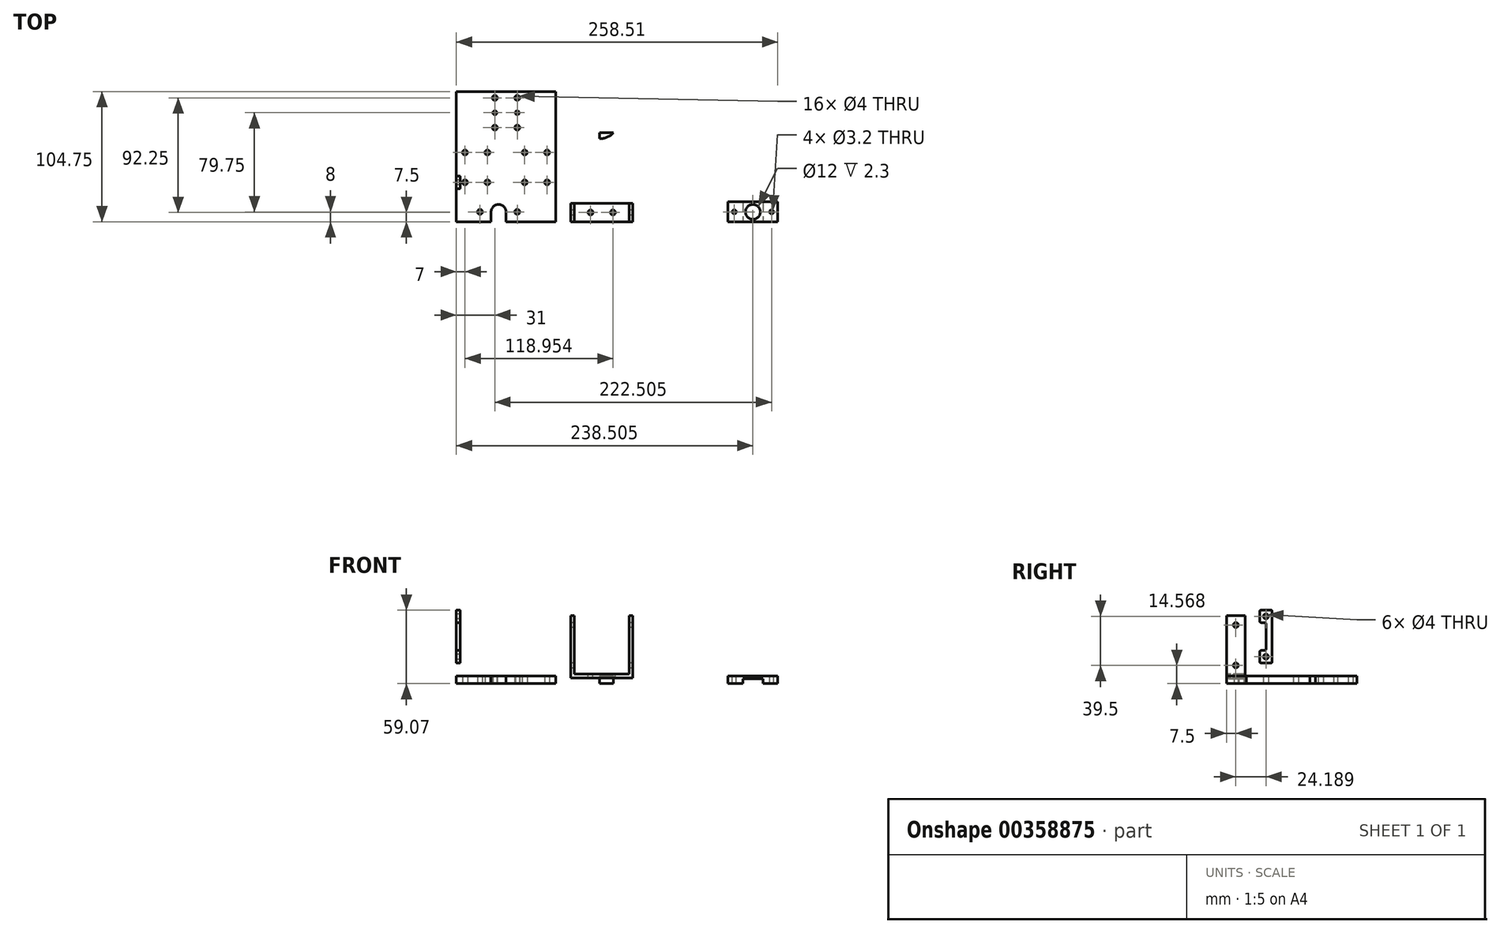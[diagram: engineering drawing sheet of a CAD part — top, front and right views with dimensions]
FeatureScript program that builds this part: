
annotation { "Feature Type Name" : "Feature", "Feature Type Description" : "" }
export const myFeature = defineFeature(function(context is Context, id is Id, definition is map)
    precondition{}
    {
        {
            var Q0;
            Q0=qCreatedBy(makeId("Front.planeOp"),FACE);
            var sketch = newSketch(context, id + "F0", { "sketchPlane" : qUnion([Q0])});
            skLineSegment(sketch, "E0", {"start": v(91.95, 4.57) * mm, "end": v(91.95, 54.57) * mm});
            skLineSegment(sketch, "E1", {"start": v(91.95, 54.57) * mm, "end": v(94.95, 54.57) * mm});
            skLineSegment(sketch, "E2", {"start": v(94.95, 54.57) * mm, "end": v(94.95, 7.57) * mm});
            skLineSegment(sketch, "E3", {"start": v(94.95, 7.57) * mm, "end": v(116.95, 7.57) * mm});
            skLineSegment(sketch, "E4", {"start": v(116.95, 4.57) * mm, "end": v(91.95, 4.57) * mm});
            skLineSegment(sketch, "E5.MirrorCS", {"start": v(138.95, 54.57) * mm, "end": v(138.95, 7.57) * mm});
            skLineSegment(sketch, "E6.MirrorCS", {"start": v(141.95, 54.57) * mm, "end": v(138.95, 54.57) * mm});
            skLineSegment(sketch, "E7.MirrorCS", {"start": v(141.95, 4.57) * mm, "end": v(141.95, 54.57) * mm});
            skLineSegment(sketch, "E8.MirrorCS", {"start": v(138.95, 7.57) * mm, "end": v(116.95, 7.57) * mm});
            skLineSegment(sketch, "E9.MirrorCS", {"start": v(116.95, 4.57) * mm, "end": v(141.95, 4.57) * mm});
            skSolve(sketch);
        }
        {
            var Q0;
            Q0=makeQuery(id+"F0.imprint","IMPRINT",FACE,{"disambiguationData":[TD([[makeQuery(id+"F0.imprint","IMPRINT",EDGE,{"derivedFrom":sQuery(id+"F0.wireOp",EDGE,"E0")}),-1.0]])]});
            extrude(context, id + "F1", {"entities" : qUnion([Q0]), "oppositeDirection" : true, "depth" : 15 * mm});
        }
        {
            var Q0;
            Q0=makeQuery(id+"F1.opExtrude","SWEPT_FACE",FACE,{"disambiguationData":[OSD([sQuery(id+"F0.wireOp",EDGE,"E3")])]});
            var sketch = newSketch(context, id + "F2", { "sketchPlane" : qUnion([Q0])});
            skCircle(sketch, "E10", {"center": v(107.95, 7.5) * mm, "radius": 2 * mm});
            skPoint(sketch, "E10.centerSnap0", {"position": v(94.95, 7.5) * mm});
            skCircle(sketch, "E11", {"center": v(125.95, 7.5) * mm, "radius": 2 * mm});
            skLineSegment(sketch, "E12", {"start": v(107.95, 7.5) * mm, "end": v(94.95, 7.5) * mm, "construction": true});
            skLineSegment(sketch, "E13", {"start": v(125.95, 7.5) * mm, "end": v(138.95, 7.5) * mm, "construction": true});
            skSolve(sketch);
        }
        {
            var Q0;
            Q0=makeQuery(id+"F1.opExtrude","SWEPT_FACE",FACE,{"disambiguationData":[OSD([sQuery(id+"F0.wireOp",EDGE,"E0")])]});
            var sketch = newSketch(context, id + "F3", { "sketchPlane" : qUnion([Q0])});
            skCircle(sketch, "E14", {"center": v(-7.5, 14.57) * mm, "radius": 2 * mm});
            skPoint(sketch, "E14.centerSnap0", {"position": v(-7.5, 7.57) * mm});
            skCircle(sketch, "E15", {"center": v(-7.5, 47.07) * mm, "radius": 2 * mm});
            skSolve(sketch);
        }
        {
            var Q0;
            Q0=makeQuery(id+"F3.imprint","IMPRINT",FACE,{"disambiguationData":[TD([[makeQuery(id+"F3.imprint","IMPRINT",EDGE,{"derivedFrom":sQuery(id+"F3.wireOp",EDGE,"E15")}),1.0]])]});
            var Q1;
            Q1=makeQuery(id+"F3.imprint","IMPRINT",FACE,{"disambiguationData":[TD([[makeQuery(id+"F3.imprint","IMPRINT",EDGE,{"derivedFrom":sQuery(id+"F3.wireOp",EDGE,"E14")}),1.0]])]});
            extrude(context, id + "F4", {"entities" : qUnion([Q0, Q1]), "operationType" : NewBodyOperationType.REMOVE, "endBound" : BoundingType.THROUGH_ALL, "oppositeDirection" : true, "depth" : 25 * mm});
        }
        {
            var Q0;
            Q0=makeQuery(id+"F2.imprint","IMPRINT",FACE,{"disambiguationData":[TD([[makeQuery(id+"F2.imprint","IMPRINT",EDGE,{"derivedFrom":sQuery(id+"F2.wireOp",EDGE,"E10")}),1.0]])]});
            var Q1;
            Q1=makeQuery(id+"F2.imprint","IMPRINT",FACE,{"disambiguationData":[TD([[makeQuery(id+"F2.imprint","IMPRINT",EDGE,{"derivedFrom":sQuery(id+"F2.wireOp",EDGE,"E11")}),1.0]])]});
            var Q2;
            Q2=sQuery(id+"F2.wireOp",EDGE,"E10");
            var Q3;
            Q3=sQuery(id+"F2.wireOp",EDGE,"E11");
            extrude(context, id + "F5", {"entities" : qUnion([Q0, Q1]), "operationType" : NewBodyOperationType.REMOVE, "surfaceEntities" : qUnion([Q2, Q3]), "endBound" : BoundingType.UP_TO_NEXT, "oppositeDirection" : true, "depth" : 25 * mm});
        }
        {
            var Q0;
            Q0=qCreatedBy(makeId("Right.planeOp"),FACE);
            var sketch = newSketch(context, id + "F6", { "sketchPlane" : qUnion([Q0])});
            skLineSegment(sketch, "E16.top", {"start": v(26.69, 16.57) * mm, "end": v(36.69, 16.57) * mm});
            skLineSegment(sketch, "E16.right", {"start": v(36.69, 59.07) * mm, "end": v(36.69, 16.57) * mm});
            skCircle(sketch, "E17", {"center": v(31.69, 54.07) * mm, "radius": 2 * mm});
            skCircle(sketch, "E18", {"center": v(31.69, 21.57) * mm, "radius": 2 * mm});
            skLineSegment(sketch, "E19", {"start": v(31.69, 49.07) * mm, "end": v(31.69, 26.57) * mm});
            skLineSegment(sketch, "E20", {"start": v(31.69, 49.07) * mm, "end": v(26.69, 49.07) * mm});
            skLineSegment(sketch, "E21", {"start": v(31.69, 26.57) * mm, "end": v(26.69, 26.57) * mm});
            skLineSegment(sketch, "E22.trimOffspring", {"start": v(26.69, 26.57) * mm, "end": v(26.69, 16.57) * mm});
            skLineSegment(sketch, "E23", {"start": v(36.69, 59.07) * mm, "end": v(26.69, 59.07) * mm});
            skLineSegment(sketch, "E24", {"start": v(26.69, 59.07) * mm, "end": v(26.69, 49.07) * mm});
            skSolve(sketch);
        }
        {
            var Q0;
            Q0=makeQuery(id+"F6.imprint","IMPRINT",FACE,{"disambiguationData":[TD([[makeQuery(id+"F6.imprint","IMPRINT",EDGE,{"derivedFrom":sQuery(id+"F6.wireOp",EDGE,"E16.top")}),1.0]])]});
            extrude(context, id + "F7", {"entities" : qUnion([Q0]), "depth" : 3 * mm});
        }
        {
            var Q0;
            Q0=makeQuery(id+"F7.opExtrude","SWEPT_EDGE",EDGE,{"disambiguationData":[OSD([sQuery(id+"F6.wireOp",EDGE,"E16.bottom"),sQuery(id+"F6.wireOp",EDGE,"E16.left")])]});
            var Q1;
            Q1=makeQuery(id+"F7.opExtrude","SWEPT_EDGE",EDGE,{"disambiguationData":[OSD([sQuery(id+"F6.wireOp",EDGE,"E16.left"),sQuery(id+"F6.wireOp",EDGE,"E20")])]});
            var Q2;
            Q2=makeQuery(id+"F7.opExtrude","SWEPT_EDGE",EDGE,{"disambiguationData":[OSD([sQuery(id+"F6.wireOp",EDGE,"E21"),sQuery(id+"F6.wireOp",EDGE,"E22.trimOffspring")])]});
            var Q3;
            Q3=makeQuery(id+"F7.opExtrude","SWEPT_EDGE",EDGE,{"disambiguationData":[OSD([sQuery(id+"F6.wireOp",EDGE,"E16.top"),sQuery(id+"F6.wireOp",EDGE,"E22.trimOffspring")])]});
            var Q4;
            Q4=makeQuery(id+"F7.opExtrude","SWEPT_EDGE",EDGE,{"disambiguationData":[OSD([sQuery(id+"F6.wireOp",EDGE,"E16.top"),sQuery(id+"F6.wireOp",EDGE,"E16.right")])]});
            var Q5;
            Q5=makeQuery(id+"F7.opExtrude","SWEPT_EDGE",EDGE,{"disambiguationData":[OSD([sQuery(id+"F6.wireOp",EDGE,"E16.bottom"),sQuery(id+"F6.wireOp",EDGE,"E16.right")])]});
            var Q6;
            Q6=makeQuery(id+"F7.opExtrude","SWEPT_EDGE",EDGE,{"disambiguationData":[OSD([sQuery(id+"F6.wireOp",EDGE,"E19"),sQuery(id+"F6.wireOp",EDGE,"E21")])]});
            var Q7;
            Q7=makeQuery(id+"F7.opExtrude","SWEPT_EDGE",EDGE,{"disambiguationData":[OSD([sQuery(id+"F6.wireOp",EDGE,"E19"),sQuery(id+"F6.wireOp",EDGE,"E20")])]});
            var Q8;
            Q8=makeQuery(id+"F7.opExtrude","SWEPT_EDGE",EDGE,{"disambiguationData":[OSD([sQuery(id+"F6.wireOp",EDGE,"E23"),sQuery(id+"F6.wireOp",EDGE,"E24")])]});
            fillet(context, id + "F8", {"entities" : qUnion([Q0, Q1, Q2, Q3, Q4, Q5, Q6, Q7, Q8]), "radius" : 1 * mm, "tangentPropagation" : true, "allowEdgeOverflow" : false});
        }
        {
            var Q0;
            Q0=qCreatedBy(makeId("Top.planeOp"),FACE);
            var sketch = newSketch(context, id + "F9", { "sketchPlane" : qUnion([Q0])});
            skLineSegment(sketch, "E25.bottom", {"start": v(7, 55.75) * mm, "end": v(25, 55.75) * mm, "construction": true});
            skLineSegment(sketch, "E25.top", {"start": v(7, 31.75) * mm, "end": v(25, 31.75) * mm, "construction": true});
            skLineSegment(sketch, "E25.left", {"start": v(7, 55.75) * mm, "end": v(7, 31.75) * mm, "construction": true});
            skLineSegment(sketch, "E25.right", {"start": v(25, 55.75) * mm, "end": v(25, 31.75) * mm, "construction": true});
            skCircle(sketch, "E26", {"center": v(7, 55.75) * mm, "radius": 2 * mm});
            skCircle(sketch, "E27", {"center": v(25, 55.75) * mm, "radius": 2 * mm});
            skCircle(sketch, "E28", {"center": v(7, 31.75) * mm, "radius": 2 * mm});
            skCircle(sketch, "E29", {"center": v(25, 31.75) * mm, "radius": 2 * mm});
            skLineSegment(sketch, "E30.bottom", {"start": v(55, 55.75) * mm, "end": v(73, 55.75) * mm, "construction": true});
            skLineSegment(sketch, "E30.top", {"start": v(55, 31.75) * mm, "end": v(73, 31.75) * mm, "construction": true});
            skLineSegment(sketch, "E30.left", {"start": v(55, 55.75) * mm, "end": v(55, 31.75) * mm, "construction": true});
            skLineSegment(sketch, "E30.right", {"start": v(73, 55.75) * mm, "end": v(73, 31.75) * mm, "construction": true});
            skCircle(sketch, "E31", {"center": v(55, 55.75) * mm, "radius": 2 * mm});
            skCircle(sketch, "E32", {"center": v(73, 55.75) * mm, "radius": 2 * mm});
            skCircle(sketch, "E33", {"center": v(55, 31.75) * mm, "radius": 2 * mm});
            skCircle(sketch, "E34", {"center": v(73, 31.75) * mm, "radius": 2 * mm});
            skLineSegment(sketch, "E35.bottom", {"start": v(31, 99.75) * mm, "end": v(49, 99.75) * mm, "construction": true});
            skLineSegment(sketch, "E35.top", {"start": v(31, 75.75) * mm, "end": v(49, 75.75) * mm, "construction": true});
            skLineSegment(sketch, "E35.left", {"start": v(31, 99.75) * mm, "end": v(31, 75.75) * mm, "construction": true});
            skLineSegment(sketch, "E35.right", {"start": v(49, 99.75) * mm, "end": v(49, 75.75) * mm, "construction": true});
            skCircle(sketch, "E36", {"center": v(31, 99.75) * mm, "radius": 2 * mm});
            skCircle(sketch, "E37", {"center": v(49, 99.75) * mm, "radius": 2 * mm});
            skCircle(sketch, "E38", {"center": v(31, 75.75) * mm, "radius": 2 * mm});
            skCircle(sketch, "E39", {"center": v(49, 75.75) * mm, "radius": 2 * mm});
            skLineSegment(sketch, "E40.bottom", {"start": v(0, 0) * mm, "end": v(80, 0) * mm});
            skLineSegment(sketch, "E40.top", {"start": v(0, 104.75) * mm, "end": v(80, 104.75) * mm});
            skLineSegment(sketch, "E40.left", {"start": v(0, 0) * mm, "end": v(0, 104.75) * mm});
            skLineSegment(sketch, "E40.right", {"start": v(80, 0) * mm, "end": v(80, 104.75) * mm});
            skCircle(sketch, "E41", {"center": v(34, 8) * mm, "radius": 6 * mm});
            skPoint(sketch, "E41.centerSnap0", {"position": v(0, 52.37) * mm});
            skPoint(sketch, "E42.centerSnap0", {"position": v(49, 87.75) * mm});
            skCircle(sketch, "E43", {"center": v(49, 87.75) * mm, "radius": 1.6 * mm});
            skPoint(sketch, "E43.centerSnap0", {"position": v(31, 87.75) * mm});
            skCircle(sketch, "E44", {"center": v(31, 87.75) * mm, "radius": 1.6 * mm});
            skPoint(sketch, "E45", {"position": v(40, 0) * mm});
            skLineSegment(sketch, "E46", {"start": v(40, 0) * mm, "end": v(40, 104.75) * mm, "construction": true});
            skLineSegment(sketch, "E47", {"start": v(31, 87.75) * mm, "end": v(0, 87.75) * mm, "construction": true});
            skLineSegment(sketch, "E48", {"start": v(49, 87.75) * mm, "end": v(80, 87.75) * mm, "construction": true});
            skLineSegment(sketch, "E49", {"start": v(28, 8) * mm, "end": v(28, 0) * mm});
            skLineSegment(sketch, "E50", {"start": v(40, 8) * mm, "end": v(40, 0) * mm});
            skCircle(sketch, "E51", {"center": v(19, 8) * mm, "radius": 2 * mm});
            skCircle(sketch, "E52", {"center": v(49, 8) * mm, "radius": 2 * mm});
            skSolve(sketch);
        }
        {
            var Q0;
            Q0=makeQuery(id+"F9.imprint","IMPRINT",FACE,{"disambiguationData":[TD([[makeQuery(id+"F9.imprint","IMPRINT",EDGE,{"derivedFrom":sQuery(id+"F9.wireOp",EDGE,"E26")}),-1.0]])]});
            extrude(context, id + "F10", {"entities" : qUnion([Q0]), "depth" : 6 * mm});
        }
        {
            var Q0;
            Q0=qCreatedBy(makeId("Top.planeOp"),FACE);
            var sketch = newSketch(context, id + "F11", { "sketchPlane" : qUnion([Q0])});
            skLineSegment(sketch, "E53.bottom", {"start": v(95.33, 71.64) * mm, "end": v(115.33, 71.64) * mm});
            skLineSegment(sketch, "E53.top", {"start": v(95.33, 61.64) * mm, "end": v(115.33, 61.64) * mm});
            skLineSegment(sketch, "E53.left", {"start": v(95.33, 71.64) * mm, "end": v(95.33, 61.64) * mm});
            skLineSegment(sketch, "E53.right", {"start": v(115.33, 71.64) * mm, "end": v(115.33, 61.64) * mm});
            skCircle(sketch, "E54", {"center": v(100.33, 66.64) * mm, "radius": 2 * mm});
            skArc(sketch, "E55", {"start": v(104.38, 71.64) * mm, "mid": v(109.37, 68.13) * mm, "end": v(115.33, 66.9) * mm});
            skArc(sketch, "E56.MirrorCS", {"start": v(126.29, 71.64) * mm, "mid": v(121.3, 68.13) * mm, "end": v(115.33, 66.9) * mm});
            skLineSegment(sketch, "E57.MirrorCS", {"start": v(135.33, 71.64) * mm, "end": v(115.33, 71.64) * mm});
            skLineSegment(sketch, "E58.MirrorCS", {"start": v(135.33, 71.64) * mm, "end": v(135.33, 61.64) * mm});
            skCircle(sketch, "E59.MirrorC", {"center": v(130.33, 66.64) * mm, "radius": 2 * mm});
            skLineSegment(sketch, "E60.MirrorCS", {"start": v(135.33, 61.64) * mm, "end": v(115.33, 61.64) * mm});
            skSolve(sketch);
        }
        {
            var Q0;
            Q0=makeQuery(id+"F11.imprint","IMPRINT",FACE,{"disambiguationData":[TD([[makeQuery(id+"F11.imprint","IMPRINT",EDGE,{"derivedFrom":sQuery(id+"F11.wireOp",EDGE,"E53.top")}),1.0]])]});
            var Q1;
            {var subQ0=sQuery(id+"F11.wireOp",EDGE,"E56.MirrorCS");Q1=makeQuery(id+"F11.imprint","IMPRINT",FACE,{"disambiguationData":[TD([[makeQuery(id+"F11.imprint","IMPRINT",EDGE,{"derivedFrom":subQ0}),1.0]])]});}
            extrude(context, id + "F12", {"entities" : qUnion([Q0, Q1]), "depth" : 6 * mm});
        }
        {
            var Q0;
            Q0=qCreatedBy(makeId("Front.planeOp"),FACE);
            var sketch = newSketch(context, id + "F13", { "sketchPlane" : qUnion([Q0])});
            skLineSegment(sketch, "E61", {"start": v(218.5, 0) * mm, "end": v(218.5, 6) * mm});
            skLineSegment(sketch, "E62", {"start": v(218.5, 6) * mm, "end": v(258.5, 6) * mm});
            skLineSegment(sketch, "E63", {"start": v(258.5, 6) * mm, "end": v(258.5, 0) * mm});
            skLineSegment(sketch, "E64", {"start": v(258.5, 0) * mm, "end": v(246.5, 0) * mm});
            skLineSegment(sketch, "E65", {"start": v(246.5, 0) * mm, "end": v(246.5, 3.7) * mm});
            skLineSegment(sketch, "E66", {"start": v(246.5, 3.7) * mm, "end": v(230.5, 3.7) * mm});
            skLineSegment(sketch, "E67", {"start": v(230.5, 3.7) * mm, "end": v(230.5, 0) * mm});
            skLineSegment(sketch, "E68", {"start": v(230.5, 0) * mm, "end": v(218.5, 0) * mm});
            skSolve(sketch);
        }
        {
            var Q0;
            Q0=makeQuery(id+"F13.imprint","IMPRINT",FACE,{"disambiguationData":[TD([[makeQuery(id+"F13.imprint","IMPRINT",EDGE,{"derivedFrom":sQuery(id+"F13.wireOp",EDGE,"E61")}),-1.0]])]});
            extrude(context, id + "F14", {"entities" : qUnion([Q0]), "oppositeDirection" : true, "depth" : 16 * mm});
        }
        {
            var Q0;
            Q0=makeQuery(id+"F14.opExtrude","SWEPT_FACE",FACE,{"disambiguationData":[OSD([sQuery(id+"F13.wireOp",EDGE,"E62")])]});
            var sketch = newSketch(context, id + "F15", { "sketchPlane" : qUnion([Q0])});
            skCircle(sketch, "E69", {"center": v(238.5, 8) * mm, "radius": 6 * mm});
            skPoint(sketch, "E69.centerSnap0", {"position": v(218.5, 8) * mm});
            skPoint(sketch, "E69.centerSnap1", {"position": v(238.5, 0) * mm});
            skCircle(sketch, "E70", {"center": v(223.5, 8) * mm, "radius": 1.6 * mm});
            skCircle(sketch, "E71", {"center": v(253.5, 8) * mm, "radius": 1.6 * mm});
            skSolve(sketch);
        }
        {
            var Q0;
            Q0=makeQuery(id+"F15.imprint","IMPRINT",FACE,{"disambiguationData":[TD([[makeQuery(id+"F15.imprint","IMPRINT",EDGE,{"derivedFrom":sQuery(id+"F15.wireOp",EDGE,"E70")}),1.0]])]});
            var Q1;
            Q1=makeQuery(id+"F15.imprint","IMPRINT",FACE,{"disambiguationData":[TD([[makeQuery(id+"F15.imprint","IMPRINT",EDGE,{"derivedFrom":sQuery(id+"F15.wireOp",EDGE,"E69")}),1.0]])]});
            var Q2;
            Q2=makeQuery(id+"F15.imprint","IMPRINT",FACE,{"disambiguationData":[TD([[makeQuery(id+"F15.imprint","IMPRINT",EDGE,{"derivedFrom":sQuery(id+"F15.wireOp",EDGE,"E71")}),1.0]])]});
            extrude(context, id + "F16", {"entities" : qUnion([Q0, Q1, Q2]), "operationType" : NewBodyOperationType.REMOVE, "endBound" : BoundingType.THROUGH_ALL, "oppositeDirection" : true, "depth" : 25 * mm});
        }
        {
            var Q0;
            Q0=makeQuery(id+"F12.opExtrude","SWEPT_BODY",BODY,{"disambiguationData":[OSD([sQuery(id+"F11.wireOp",EDGE,"E53.bottom"),sQuery(id+"F11.wireOp",EDGE,"E53.top"),sQuery(id+"F11.wireOp",EDGE,"E53.left"),sQuery(id+"F11.wireOp",EDGE,"E54"),sQuery(id+"F11.wireOp",EDGE,"E55"),sQuery(id+"F11.wireOp",EDGE,"E56.MirrorCS"),sQuery(id+"F11.wireOp",EDGE,"E57.MirrorCS"),sQuery(id+"F11.wireOp",EDGE,"E58.MirrorCS"),sQuery(id+"F11.wireOp",EDGE,"E59.MirrorC"),sQuery(id+"F11.wireOp",EDGE,"E60.MirrorCS")])]});
            deleteBodies(context, id + "F17", {"entities" : qUnion([Q0])});
        }
    });
